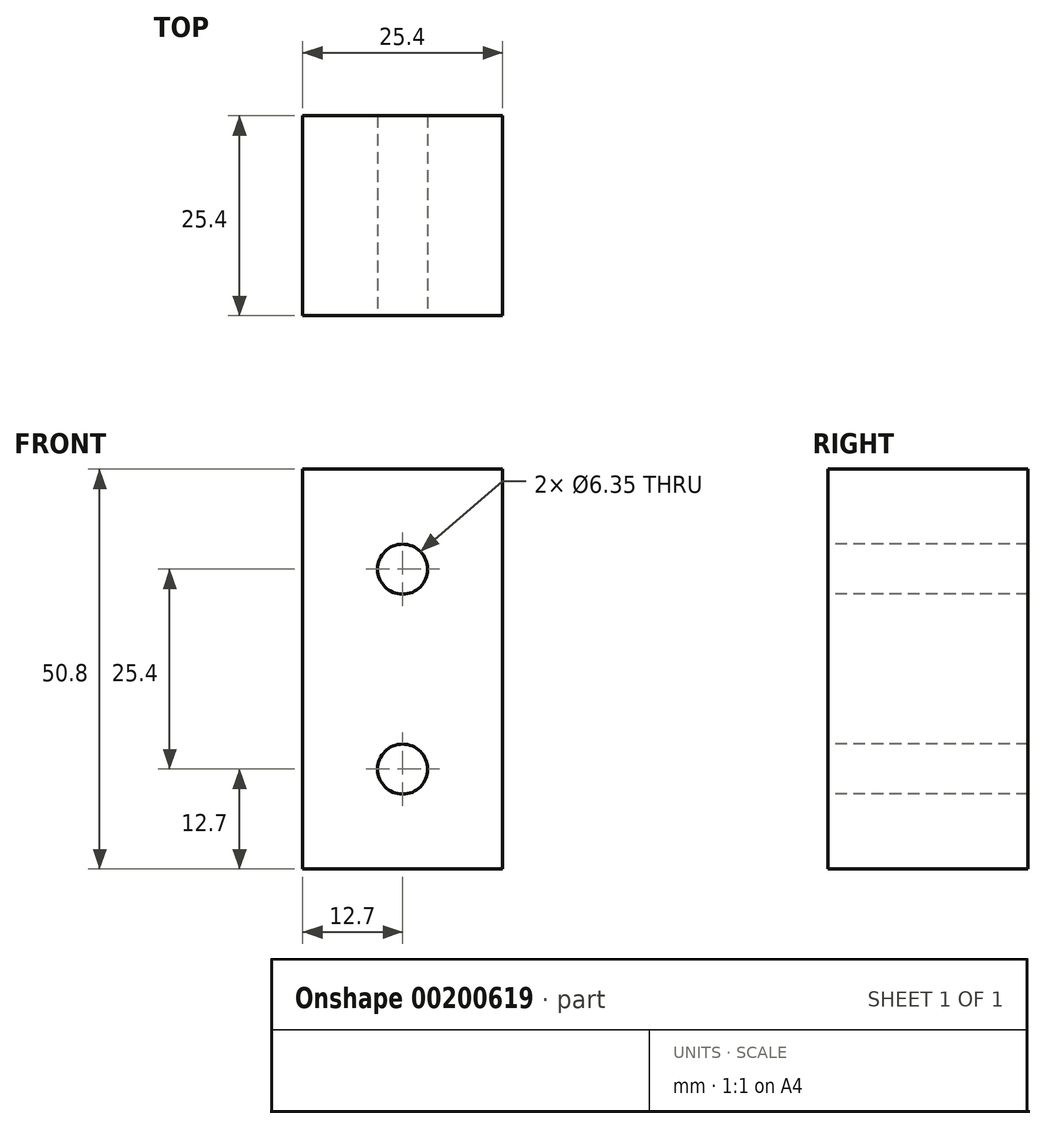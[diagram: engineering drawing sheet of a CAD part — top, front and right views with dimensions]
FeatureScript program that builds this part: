
annotation { "Feature Type Name" : "Feature", "Feature Type Description" : "" }
export const myFeature = defineFeature(function(context is Context, id is Id, definition is map)
    precondition{}
    {
        {
            var Q0;
            Q0=qCreatedBy(makeId("Front.planeOp"),FACE);
            var sketch = newSketch(context, id + "F0", { "sketchPlane" : qUnion([Q0])});
            skLineSegment(sketch, "E0.bottom", {"start": v(0, 0) * mm, "end": v(25.4, 0) * mm});
            skLineSegment(sketch, "E0.top", {"start": v(0, 50.8) * mm, "end": v(25.4, 50.8) * mm});
            skLineSegment(sketch, "E0.left", {"start": v(0, 0) * mm, "end": v(0, 50.8) * mm});
            skLineSegment(sketch, "E0.right", {"start": v(25.4, 0) * mm, "end": v(25.4, 50.8) * mm});
            skSolve(sketch);
        }
        {
            var Q0;
            Q0=makeQuery(id+"F0.imprint","IMPRINT",FACE,{"disambiguationData":[TD([[makeQuery(id+"F0.imprint","IMPRINT",EDGE,{"derivedFrom":sQuery(id+"F0.wireOp",EDGE,"E0.bottom")}),1.0]])]});
            extrude(context, id + "F1", {"entities" : qUnion([Q0]), "depth" : 25.4 * mm});
        }
        {
            var Q0;
            Q0=makeQuery(id+"F1.opExtrude","CAP_FACE",FACE,{"disambiguationData":[OSD([sQuery(id+"F0.wireOp",EDGE,"E0.bottom"),sQuery(id+"F0.wireOp",EDGE,"E0.top"),sQuery(id+"F0.wireOp",EDGE,"E0.left"),sQuery(id+"F0.wireOp",EDGE,"E0.right")])],"isStart":false});
            var sketch = newSketch(context, id + "F2", { "sketchPlane" : qUnion([Q0])});
            skLineSegment(sketch, "E1.0.0", {"start": v(0, 50.8) * mm, "end": v(0, 0) * mm});
            skLineSegment(sketch, "E1.0.1", {"start": v(0, 0) * mm, "end": v(25.4, 0) * mm});
            skLineSegment(sketch, "E1.0.2", {"start": v(25.4, 0) * mm, "end": v(25.4, 50.8) * mm});
            skLineSegment(sketch, "E1.0.3", {"start": v(25.4, 50.8) * mm, "end": v(0, 50.8) * mm});
            skPoint(sketch, "E2", {"position": v(12.7, 38.1) * mm});
            skPoint(sketch, "E3", {"position": v(12.7, 12.7) * mm});
            skLineSegment(sketch, "E4", {"start": v(12.7, 38.1) * mm, "end": v(12.7, 12.7) * mm, "construction": true});
            skSolve(sketch);
        }
        {
            var Q0;
            Q0=sQuery(id+"F2.wireOp",VERTEX,"E2");
            var Q1;
            Q1=sQuery(id+"F2.wireOp",VERTEX,"E3");
            var Q2;
            Q2=makeQuery(id+"F1.opExtrude","SWEPT_BODY",BODY,{"disambiguationData":[OSD([sQuery(id+"F0.wireOp",EDGE,"E0.bottom"),sQuery(id+"F0.wireOp",EDGE,"E0.top"),sQuery(id+"F0.wireOp",EDGE,"E0.left"),sQuery(id+"F0.wireOp",EDGE,"E0.right")])]});
            hole(context, id + "F3", {"style" : HoleStyle.SIMPLE, "endStyle" : HoleEndStyle.THROUGH, "holeDiameter" : 6.35 * mm, "locations" : qUnion([Q0, Q1]), "scope" : qUnion([Q2]), "isTappedThrough" : true});
        }
    });
